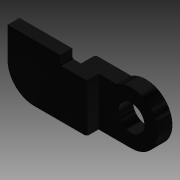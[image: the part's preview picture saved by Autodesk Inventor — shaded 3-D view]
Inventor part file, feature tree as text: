
AUTODESK INVENTOR PART (.ipt)
format: ipt  version: 2013 (Build 170138000, 138)  size: 105,472 bytes
history: native  units: in
note: dims shown in document units (in); Inventor stores cm internally (conversion verified against a paired STEP export)
features: other x1, imported_body x1, extrude x1, sketch x1
ambient origin geometry x8: Origin, YZ Plane, XZ Plane, XY Plane, X Axis, Y Axis, Z Axis, Center Point
feature tree (4):
  other  "TETRIX_TT_LINK_1_2011"
  imported_body  "Base1"
  extrude  "Extrusion1"  [1 undecoded]
  sketch  "Sketch1"  dims[d0=0.006in d1=0.0in]
note: 1 required parameter value undecoded (feature->parameter linkage not recoverable at this tier; creation-order binding heuristic only, values carry confidence <= 0.55)
